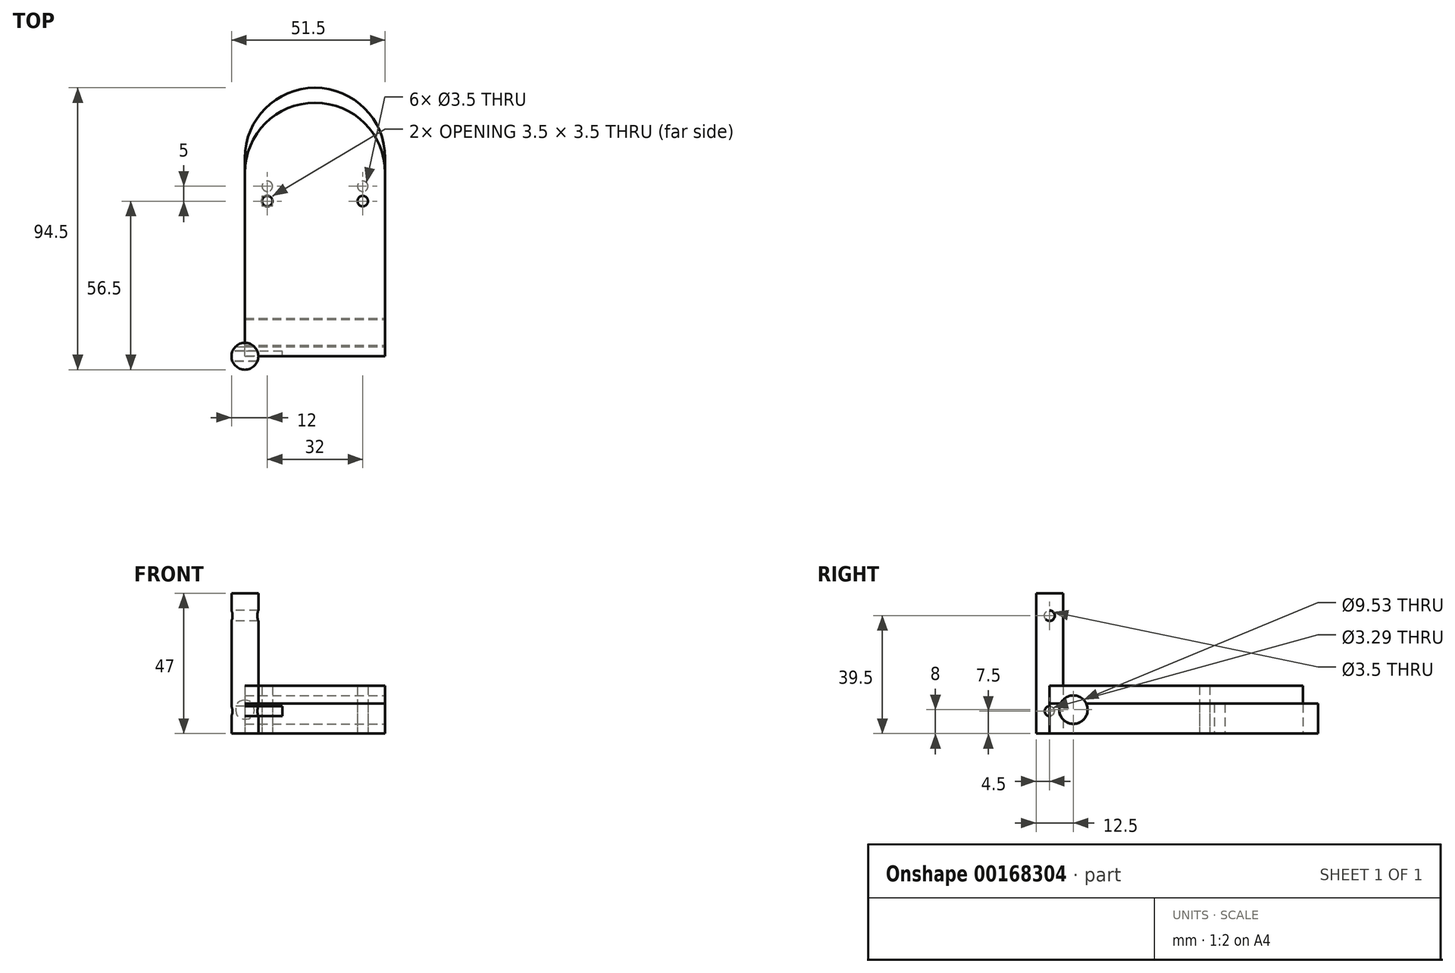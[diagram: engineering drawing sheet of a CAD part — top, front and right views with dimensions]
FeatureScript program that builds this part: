
annotation { "Feature Type Name" : "Feature", "Feature Type Description" : "" }
export const myFeature = defineFeature(function(context is Context, id is Id, definition is map)
    precondition{}
    {
        {
            var Q0;
            Q0=qCreatedBy(makeId("Top.planeOp"),FACE);
            var sketch = newSketch(context, id + "F0", { "sketchPlane" : qUnion([Q0])});
            skLineSegment(sketch, "E0.bottom", {"start": v(0, 0) * mm, "end": v(47, 0) * mm});
            skLineSegment(sketch, "E0.left", {"start": v(0, 0) * mm, "end": v(0, 66.5) * mm});
            skLineSegment(sketch, "E0.right", {"start": v(47, 0) * mm, "end": v(47, 66.5) * mm});
            skArc(sketch, "E1", {"start": v(47, 66.5) * mm, "mid": v(23.5, 90) * mm, "end": v(0, 66.5) * mm});
            skSolve(sketch);
        }
        {
            var Q0;
            Q0=makeQuery(id+"F0.imprint","IMPRINT",FACE,{"disambiguationData":[TD([[makeQuery(id+"F0.imprint","IMPRINT",EDGE,{"derivedFrom":sQuery(id+"F0.wireOp",EDGE,"E0.bottom")}),1.0]])]});
            extrude(context, id + "F1", {"entities" : qUnion([Q0]), "depth" : 10 * mm});
        }
        {
            var Q0;
            Q0=makeQuery(id+"F1.opExtrude","CAP_FACE",FACE,{"disambiguationData":[OSD([sQuery(id+"F0.wireOp",EDGE,"E0.bottom"),sQuery(id+"F0.wireOp",EDGE,"E0.left"),sQuery(id+"F0.wireOp",EDGE,"E0.right"),sQuery(id+"F0.wireOp",EDGE,"E1")])],"isStart":true});
            var sketch = newSketch(context, id + "F2", { "sketchPlane" : qUnion([Q0])});
            skCircle(sketch, "E2", {"center": v(39.5, -57) * mm, "radius": 1.75 * mm});
            skCircle(sketch, "E3", {"center": v(7.5, -57) * mm, "radius": 1.75 * mm});
            skLineSegment(sketch, "E4", {"start": v(39.5, -57) * mm, "end": v(7.5, -57) * mm, "construction": true});
            skSolve(sketch);
        }
        {
            var Q0;
            Q0=makeQuery(id+"F2.imprint","IMPRINT",FACE,{"disambiguationData":[TD([[makeQuery(id+"F2.imprint","IMPRINT",EDGE,{"derivedFrom":sQuery(id+"F2.wireOp",EDGE,"E2")}),1.0]])]});
            var Q1;
            Q1=makeQuery(id+"F2.imprint","IMPRINT",FACE,{"disambiguationData":[TD([[makeQuery(id+"F2.imprint","IMPRINT",EDGE,{"derivedFrom":sQuery(id+"F2.wireOp",EDGE,"E3")}),1.0]])]});
            extrude(context, id + "F3", {"entities" : qUnion([Q0, Q1]), "operationType" : NewBodyOperationType.REMOVE, "oppositeDirection" : true, "depth" : 25 * mm});
        }
        {
            var Q0;
            Q0=makeQuery(id+"F1.opExtrude","SWEPT_BODY",BODY,{"disambiguationData":[OSD([sQuery(id+"F0.wireOp",EDGE,"E0.bottom"),sQuery(id+"F0.wireOp",EDGE,"E0.left"),sQuery(id+"F0.wireOp",EDGE,"E0.right"),sQuery(id+"F0.wireOp",EDGE,"E1")])]});
            transform(context, id + "F4", {"entities" : qUnion([Q0]), "transformType" : TransformType.TRANSLATION_3D, "dx" : 0 * mm, "dy" : 0 * mm, "dz" : 33 * mm, "makeCopy" : true});
        }
        {
            var Q0;
            Q0=makeQuery(id+"F4.opPattern","COPY",BODY,{"derivedFrom":makeQuery(id+"F1.opExtrude","SWEPT_BODY",BODY,{"disambiguationData":[OSD([sQuery(id+"F0.wireOp",EDGE,"E0.bottom"),sQuery(id+"F0.wireOp",EDGE,"E0.left"),sQuery(id+"F0.wireOp",EDGE,"E0.right"),sQuery(id+"F0.wireOp",EDGE,"E1")])]}),"instanceName":"1"});
            deleteBodies(context, id + "F5", {"entities" : qUnion([Q0])});
        }
        {
            var Q0;
            Q0=qCreatedBy(makeId("Top.planeOp"),FACE);
            var sketch = newSketch(context, id + "F6", { "sketchPlane" : qUnion([Q0])});
            skLineSegment(sketch, "E5.bottom", {"start": v(0, 0) * mm, "end": v(47, 0) * mm});
            skLineSegment(sketch, "E5.left", {"start": v(0, 0) * mm, "end": v(0, 61.5) * mm});
            skLineSegment(sketch, "E5.right", {"start": v(47, 0) * mm, "end": v(47, 61.5) * mm});
            skArc(sketch, "E6", {"start": v(47, 61.5) * mm, "mid": v(23.5, 85) * mm, "end": v(0, 61.5) * mm});
            skSolve(sketch);
        }
        {
            var Q0;
            Q0 = qSketchRegion(id + "F6", true);
            extrude(context, id + "F7", {"entities" : qUnion([Q0]), "depth" : 16 * mm});
        }
        {
            var Q0;
            Q0=makeQuery(id+"F2.imprint","IMPRINT",FACE,{"disambiguationData":[TD([[makeQuery(id+"F2.imprint","IMPRINT",EDGE,{"derivedFrom":sQuery(id+"F2.wireOp",EDGE,"E2")}),-1.0]])]});
            var sketch = newSketch(context, id + "F8", { "sketchPlane" : qUnion([Q0])});
            skLineSegment(sketch, "E7", {"start": v(39.5, -52) * mm, "end": v(7.5, -52) * mm});
            skCircle(sketch, "E8", {"center": v(39.5, -52) * mm, "radius": 1.75 * mm});
            skCircle(sketch, "E9", {"center": v(7.5, -52) * mm, "radius": 1.75 * mm});
            skSolve(sketch);
        }
        {
            var Q0;
            Q0 = qSketchRegion(id + "F8", true);
            extrude(context, id + "F9", {"entities" : qUnion([Q0]), "operationType" : NewBodyOperationType.REMOVE, "oppositeDirection" : true, "depth" : 25 * mm});
        }
        {
            var Q0;
            Q0=qCreatedBy(makeId("Top.planeOp"),FACE);
            var sketch = newSketch(context, id + "F10", { "sketchPlane" : qUnion([Q0])});
            skCircle(sketch, "E10", {"center": v(0, 0) * mm, "radius": 4.5 * mm});
            skSolve(sketch);
        }
        {
            var Q0;
            Q0=makeQuery(id+"F10.imprint","IMPRINT",FACE,{"disambiguationData":[TD([[makeQuery(id+"F10.imprint","IMPRINT",EDGE,{"derivedFrom":sQuery(id+"F10.wireOp",EDGE,"E10")}),1.0]])]});
            extrude(context, id + "F11", {"entities" : qUnion([Q0]), "depth" : 47 * mm});
        }
        {
            var Q0;
            Q0=qCreatedBy(makeId("Right.planeOp"),FACE);
            var sketch = newSketch(context, id + "F12", { "sketchPlane" : qUnion([Q0])});
            skLineSegment(sketch, "E11", {"start": v(0, 0) * mm, "end": v(0, 40.35) * mm});
            skCircle(sketch, "E12", {"center": v(0, 39.5) * mm, "radius": 1.75 * mm});
            skCircle(sketch, "E13", {"center": v(0, 7.5) * mm, "radius": 1.64 * mm});
            skSolve(sketch);
        }
        {
            var Q0;
            Q0 = qSketchRegion(id + "F12", true);
            extrude(context, id + "F13", {"entities" : qUnion([Q0]), "operationType" : NewBodyOperationType.REMOVE, "endBound" : BoundingType.SYMMETRIC, "depth" : 25 * mm});
        }
        {
            var Q0;
            Q0=makeQuery(id+"F7.opExtrude","SWEPT_FACE",FACE,{"disambiguationData":[OSD([sQuery(id+"F6.wireOp",EDGE,"E5.right")])]});
            var sketch = newSketch(context, id + "F14", { "sketchPlane" : qUnion([Q0])});
            skCircle(sketch, "E14", {"center": v(8, 8) * mm, "radius": 4.76 * mm});
            skSolve(sketch);
        }
        {
            var Q0;
            Q0=makeQuery(id+"F14.imprint","IMPRINT",FACE,{"disambiguationData":[TD([[makeQuery(id+"F14.imprint","IMPRINT",EDGE,{"derivedFrom":sQuery(id+"F14.wireOp",EDGE,"E14")}),1.0]])]});
            extrude(context, id + "F15", {"entities" : qUnion([Q0]), "operationType" : NewBodyOperationType.REMOVE, "endBound" : BoundingType.THROUGH_ALL, "oppositeDirection" : true, "depth" : 25 * mm});
        }
    });
